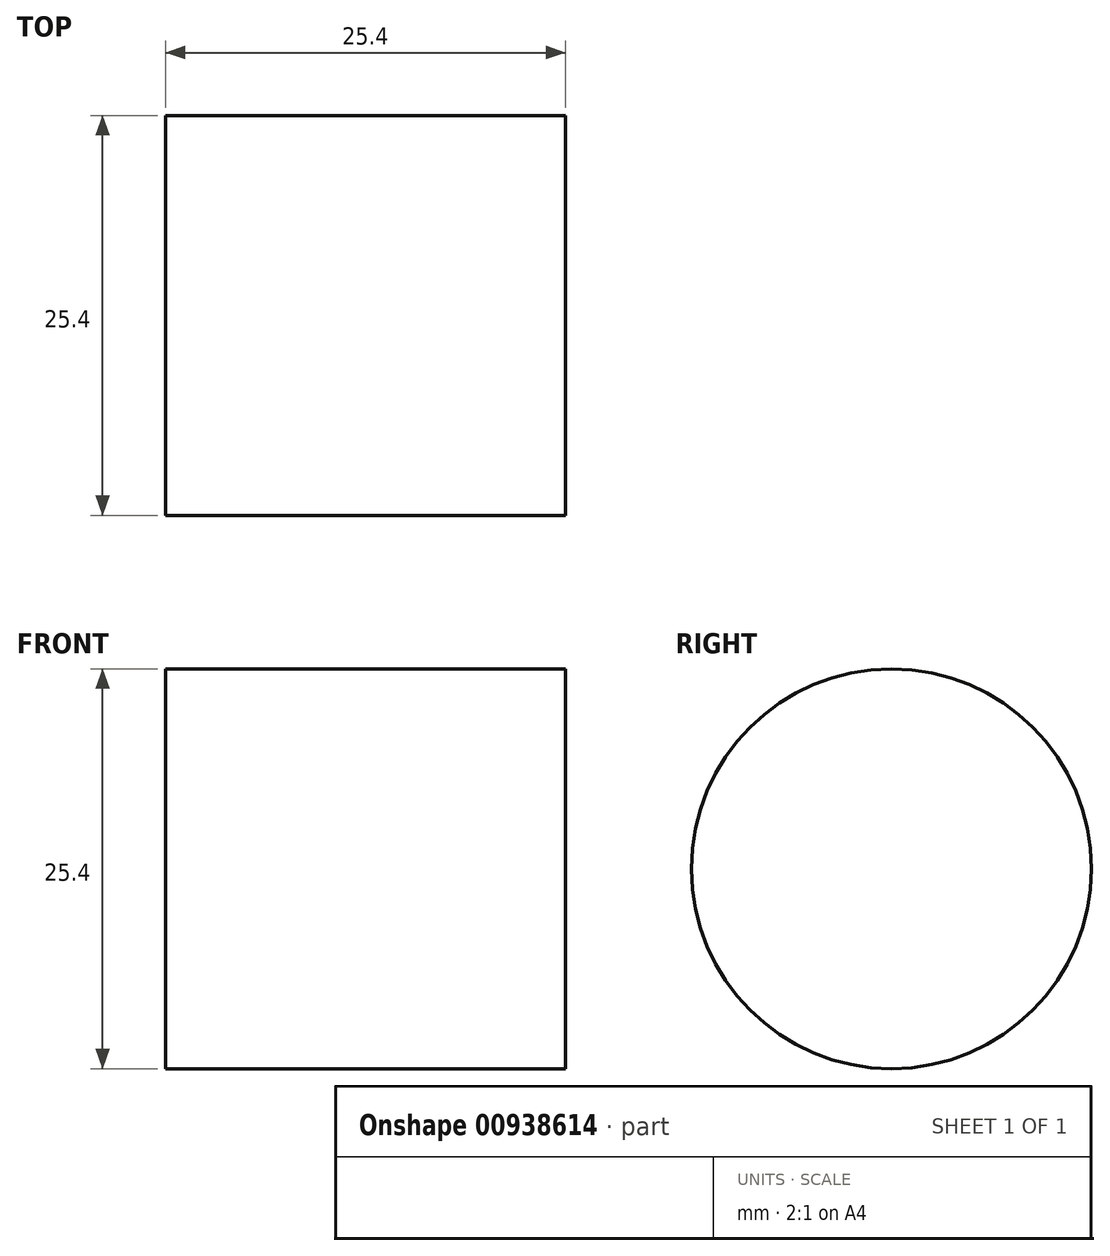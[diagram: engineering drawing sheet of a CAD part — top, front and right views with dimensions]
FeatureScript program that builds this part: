
annotation { "Feature Type Name" : "Feature", "Feature Type Description" : "" }
export const myFeature = defineFeature(function(context is Context, id is Id, definition is map)
    precondition{}
    {
        {
            var Q0;
            Q0=qCreatedBy(makeId("Right.planeOp"),FACE);
            var sketch = newSketch(context, id + "F0", { "sketchPlane" : qUnion([Q0])});
            skCircle(sketch, "E0", {"center": v(0, 0) * mm, "radius": 12.7 * mm});
            skSolve(sketch);
        }
        {
            var Q0;
            Q0=makeQuery(id+"F0.imprint","IMPRINT",FACE,{"disambiguationData":[TD([[makeQuery(id+"F0.imprint","IMPRINT",EDGE,{"derivedFrom":sQuery(id+"F0.wireOp",EDGE,"E0")}),1.0]])]});
            extrude(context, id + "F1", {"entities" : qUnion([Q0]), "oppositeDirection" : true, "depth" : 25.4 * mm, "offsetDistance" : 25.4 * mm});
        }
    });
